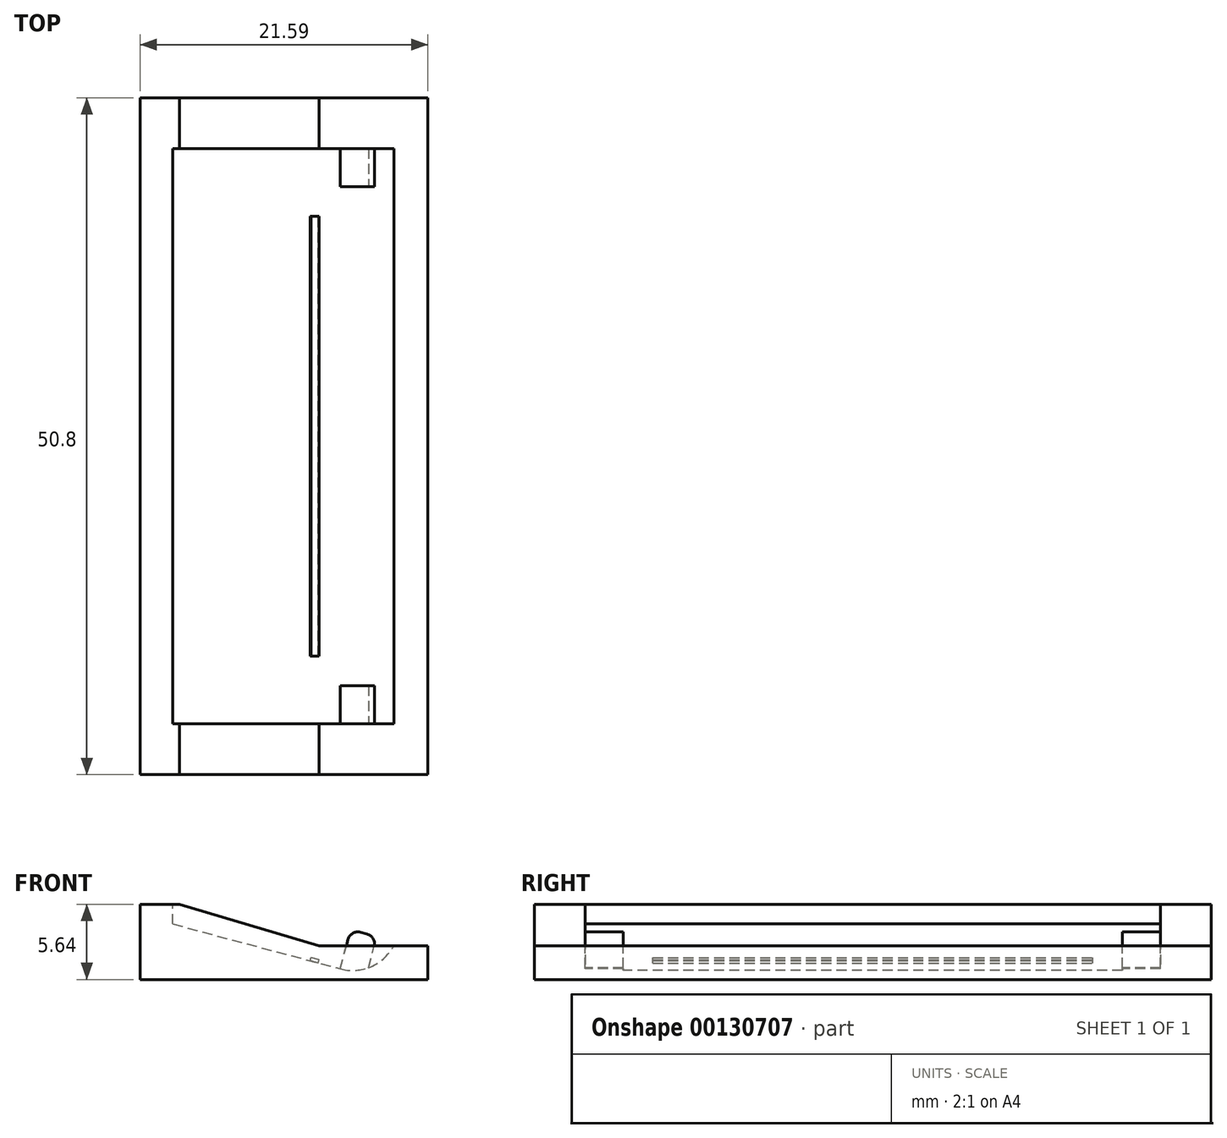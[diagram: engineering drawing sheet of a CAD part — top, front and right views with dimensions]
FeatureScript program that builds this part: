
annotation { "Feature Type Name" : "Feature", "Feature Type Description" : "" }
export const myFeature = defineFeature(function(context is Context, id is Id, definition is map)
    precondition{}
    {
        {
            var Q0;
            Q0=qCreatedBy(makeId("Top.planeOp"),FACE);
            var sketch = newSketch(context, id + "F0", { "sketchPlane" : qUnion([Q0])});
            skLineSegment(sketch, "E0.bottom", {"start": v(0, -25.4) * mm, "end": v(21.6, -25.4) * mm});
            skLineSegment(sketch, "E0.top", {"start": v(0, 25.4) * mm, "end": v(21.6, 25.4) * mm});
            skLineSegment(sketch, "E0.left", {"start": v(0, -25.4) * mm, "end": v(0, 25.4) * mm});
            skLineSegment(sketch, "E0.right", {"start": v(21.6, -25.4) * mm, "end": v(21.6, 25.4) * mm});
            skSolve(sketch);
        }
        {
            var Q0;
            Q0=makeQuery(id+"F0.imprint","IMPRINT",FACE,{"disambiguationData":[TD([[makeQuery(id+"F0.imprint","IMPRINT",EDGE,{"derivedFrom":sQuery(id+"F0.wireOp",EDGE,"E0.bottom")}),1.0]])]});
            extrude(context, id + "F1", {"entities" : qUnion([Q0]), "depth" : 2.54 * mm});
        }
        {
            var Q0;
            Q0=qCreatedBy(makeId("Front.planeOp"),FACE);
            var sketch = newSketch(context, id + "F2", { "sketchPlane" : qUnion([Q0])});
            skLineSegment(sketch, "E1", {"start": v(13.72, 2.54) * mm, "end": v(13.37, 1.24) * mm});
            skLineSegment(sketch, "E2", {"start": v(13.37, 1.24) * mm, "end": v(15.01, 0.8) * mm});
            skLineSegment(sketch, "E3", {"start": v(13.72, 2.54) * mm, "end": v(19.05, 2.54) * mm});
            skArc(sketch, "E4", {"start": v(15.01, 0.8) * mm, "mid": v(17.33, 0.97) * mm, "end": v(19.05, 2.54) * mm});
            skSolve(sketch);
        }
        {
            var Q0;
            Q0 = qSketchRegion(id + "F2", true);
            extrude(context, id + "F3", {"entities" : qUnion([Q0]), "operationType" : NewBodyOperationType.REMOVE, "endBound" : BoundingType.SYMMETRIC, "oppositeDirection" : true, "depth" : 43.18 * mm});
        }
        {
            var Q0;
            Q0=qCreatedBy(makeId("Front.planeOp"),FACE);
            var sketch = newSketch(context, id + "F4", { "sketchPlane" : qUnion([Q0])});
            skLineSegment(sketch, "E5.bottom", {"start": v(15.01, 0.8) * mm, "end": v(16.97, 0.27) * mm});
            skLineSegment(sketch, "E5.top", {"start": v(15.8, 3.74) * mm, "end": v(17.76, 3.22) * mm});
            skLineSegment(sketch, "E5.left", {"start": v(15.01, 0.8) * mm, "end": v(15.8, 3.74) * mm});
            skLineSegment(sketch, "E5.right", {"start": v(16.97, 0.27) * mm, "end": v(17.76, 3.22) * mm});
            skSolve(sketch);
        }
        {
            var Q0;
            Q0=makeQuery(id+"F4.imprint","IMPRINT",FACE,{"disambiguationData":[TD([[makeQuery(id+"F4.imprint","IMPRINT",EDGE,{"derivedFrom":sQuery(id+"F4.wireOp",EDGE,"E5.bottom")}),1.0]])]});
            extrude(context, id + "F5", {"entities" : qUnion([Q0]), "operationType" : NewBodyOperationType.ADD, "endBound" : BoundingType.SYMMETRIC, "depth" : 43.18 * mm});
        }
        {
            var Q0;
            Q0=makeQuery(id+"F5.opExtrude","SWEPT_EDGE",EDGE,{"disambiguationData":[OSD([sQuery(id+"F4.wireOp",EDGE,"E5.top"),sQuery(id+"F4.wireOp",EDGE,"E5.left")])]});
            var Q1;
            Q1=makeQuery(id+"F5.opExtrude","SWEPT_EDGE",EDGE,{"disambiguationData":[OSD([sQuery(id+"F4.wireOp",EDGE,"E5.top"),sQuery(id+"F4.wireOp",EDGE,"E5.right")])]});
            fillet(context, id + "F6", {"entities" : qUnion([Q0, Q1]), "radius" : 0.76 * mm, "tangentPropagation" : true, "allowEdgeOverflow" : false});
        }
        {
            var Q0;
            Q0=qCreatedBy(makeId("Front.planeOp"),FACE);
            var sketch = newSketch(context, id + "F7", { "sketchPlane" : qUnion([Q0])});
            skLineSegment(sketch, "E6", {"start": v(13.72, 2.54) * mm, "end": v(13.37, 1.24) * mm});
            skLineSegment(sketch, "E7", {"start": v(13.37, 1.24) * mm, "end": v(15.01, 0.8) * mm});
            skLineSegment(sketch, "E8", {"start": v(13.72, 2.54) * mm, "end": v(19.05, 2.54) * mm});
            skArc(sketch, "E9", {"start": v(15.01, 0.8) * mm, "mid": v(17.33, 0.97) * mm, "end": v(19.05, 2.54) * mm});
            skLineSegment(sketch, "E10.left", {"start": v(13.72, 2.54) * mm, "end": v(13.72, 2.54) * mm});
            skLineSegment(sketch, "E10.right", {"start": v(19.05, 2.54) * mm, "end": v(19.05, 2.54) * mm});
            skLineSegment(sketch, "E11.top", {"start": v(13.72, 7.75) * mm, "end": v(19.05, 7.75) * mm});
            skLineSegment(sketch, "E11.left", {"start": v(13.72, 2.54) * mm, "end": v(13.72, 7.75) * mm});
            skLineSegment(sketch, "E11.right", {"start": v(19.05, 2.54) * mm, "end": v(19.05, 7.75) * mm});
            skSolve(sketch);
        }
        {
            var Q0;
            Q0 = qSketchRegion(id + "F7", true);
            extrude(context, id + "F8", {"entities" : qUnion([Q0]), "operationType" : NewBodyOperationType.REMOVE, "endBound" : BoundingType.SYMMETRIC, "oppositeDirection" : true, "depth" : 37.47 * mm});
        }
        {
            var Q0;
            Q0=makeQuery(id+"F1.opExtrude","SWEPT_FACE",FACE,{"disambiguationData":[OSD([sQuery(id+"F0.wireOp",EDGE,"E0.bottom")])]});
            var sketch = newSketch(context, id + "F9", { "sketchPlane" : qUnion([Q0])});
            skLineSegment(sketch, "E12", {"start": v(13.42, 2.54) * mm, "end": v(0, 2.54) * mm});
            skLineSegment(sketch, "E13", {"start": v(0, 2.54) * mm, "end": v(0, 5.64) * mm});
            skLineSegment(sketch, "E14", {"start": v(2.94, 5.64) * mm, "end": v(13.42, 2.54) * mm});
            skPoint(sketch, "E15", {"position": v(2.94, 5.64) * mm});
            skLineSegment(sketch, "E16", {"start": v(0, 5.64) * mm, "end": v(2.94, 5.64) * mm});
            skSolve(sketch);
        }
        {
            var Q0;
            Q0=makeQuery(id+"F9.imprint","IMPRINT",FACE,{"disambiguationData":[TD([[makeQuery(id+"F9.imprint","IMPRINT",EDGE,{"derivedFrom":sQuery(id+"F9.wireOp",EDGE,"E12")}),1.0]])]});
            extrude(context, id + "F10", {"entities" : qUnion([Q0]), "operationType" : NewBodyOperationType.ADD, "oppositeDirection" : true, "depth" : 50.8 * mm});
        }
        {
            var Q0;
            Q0=qCreatedBy(makeId("Front.planeOp"),FACE);
            var sketch = newSketch(context, id + "F11", { "sketchPlane" : qUnion([Q0])});
            skLineSegment(sketch, "E17", {"start": v(15.01, 0.8) * mm, "end": v(2.45, 4.17) * mm});
            skLineSegment(sketch, "E18", {"start": v(2.45, 4.17) * mm, "end": v(2.45, 10.93) * mm});
            skLineSegment(sketch, "E19", {"start": v(2.45, 10.93) * mm, "end": v(15.01, 10.93) * mm});
            skLineSegment(sketch, "E20", {"start": v(15.01, 10.93) * mm, "end": v(15.01, 0.8) * mm});
            skSolve(sketch);
        }
        {
            var Q0;
            Q0=makeQuery(id+"F11.imprint","IMPRINT",FACE,{"disambiguationData":[TD([[makeQuery(id+"F11.imprint","IMPRINT",EDGE,{"derivedFrom":sQuery(id+"F11.wireOp",EDGE,"E17")}),-1.0]])]});
            extrude(context, id + "F12", {"entities" : qUnion([Q0]), "operationType" : NewBodyOperationType.REMOVE, "endBound" : BoundingType.SYMMETRIC, "depth" : 43.18 * mm});
        }
        {
            var Q0;
            Q0=qCreatedBy(makeId("Front.planeOp"),FACE);
            var sketch = newSketch(context, id + "F13", { "sketchPlane" : qUnion([Q0])});
            skLineSegment(sketch, "E21.bottom", {"start": v(13.37, 1.24) * mm, "end": v(12.75, 1.4) * mm});
            skLineSegment(sketch, "E21.top", {"start": v(13.43, 1.49) * mm, "end": v(12.82, 1.65) * mm});
            skLineSegment(sketch, "E21.left", {"start": v(13.37, 1.24) * mm, "end": v(13.43, 1.49) * mm});
            skLineSegment(sketch, "E21.right", {"start": v(12.75, 1.4) * mm, "end": v(12.82, 1.65) * mm});
            skSolve(sketch);
        }
        {
            var Q0;
            Q0 = qSketchRegion(id + "F13", true);
            extrude(context, id + "F14", {"entities" : qUnion([Q0]), "operationType" : NewBodyOperationType.ADD, "endBound" : BoundingType.SYMMETRIC, "depth" : 33.02 * mm});
        }
    });
